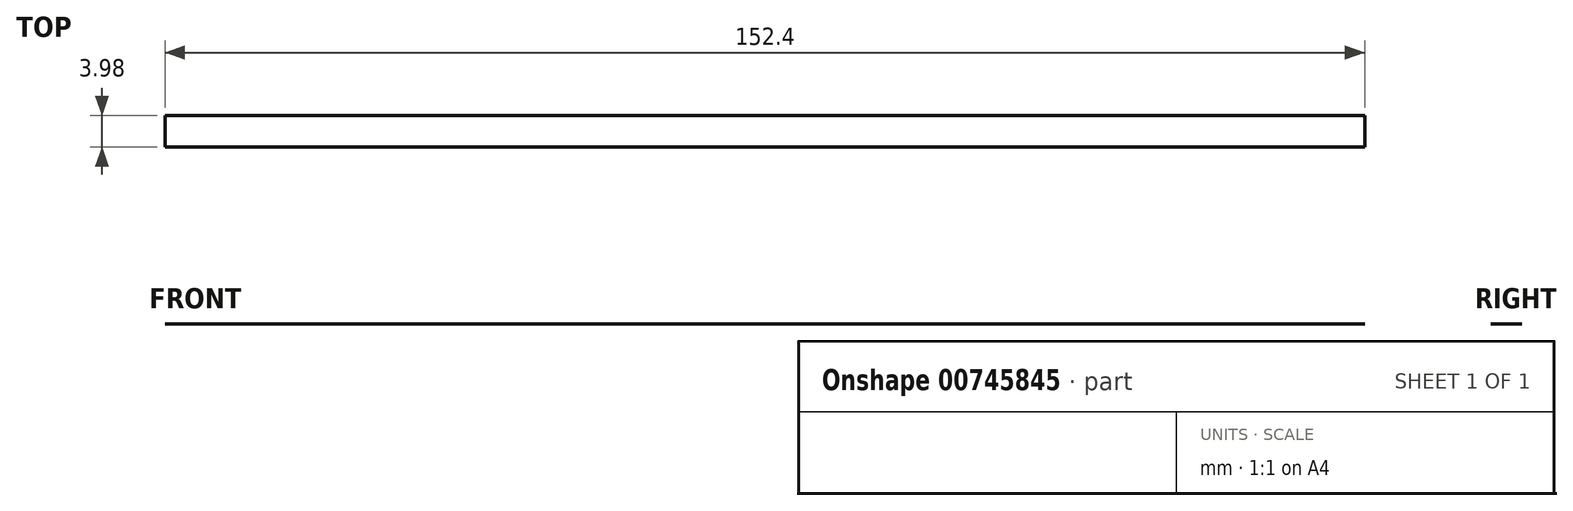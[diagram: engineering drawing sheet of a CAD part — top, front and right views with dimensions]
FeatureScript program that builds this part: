
annotation { "Feature Type Name" : "Feature", "Feature Type Description" : "" }
export const myFeature = defineFeature(function(context is Context, id is Id, definition is map)
    precondition{}
    {
        {
            var Q0;
            Q0=qCreatedBy(makeId("Front.planeOp"),FACE);
            var sketch = newSketch(context, id + "F0", { "sketchPlane" : qUnion([Q0])});
            skLineSegment(sketch, "E0", {"start": v(-75.68, 0) * mm, "end": v(76.72, 0) * mm});
            skLineSegment(sketch, "E1", {"start": v(-75.68, 0) * mm, "end": v(0, -58.82) * mm});
            skLineSegment(sketch, "E2", {"start": v(0, -58.82) * mm, "end": v(76.72, 0) * mm});
            skSolve(sketch);
        }
        {
            var Q0;
            Q0=sQuery(id+"F0.wireOp",EDGE,"E0");
            extrude(context, id + "F1", {"bodyType" : ToolBodyType.SURFACE, "surfaceEntities" : qUnion([Q0]), "depth" : 3.98 * mm, "offsetDistance" : 25.4 * mm});
        }
    });
